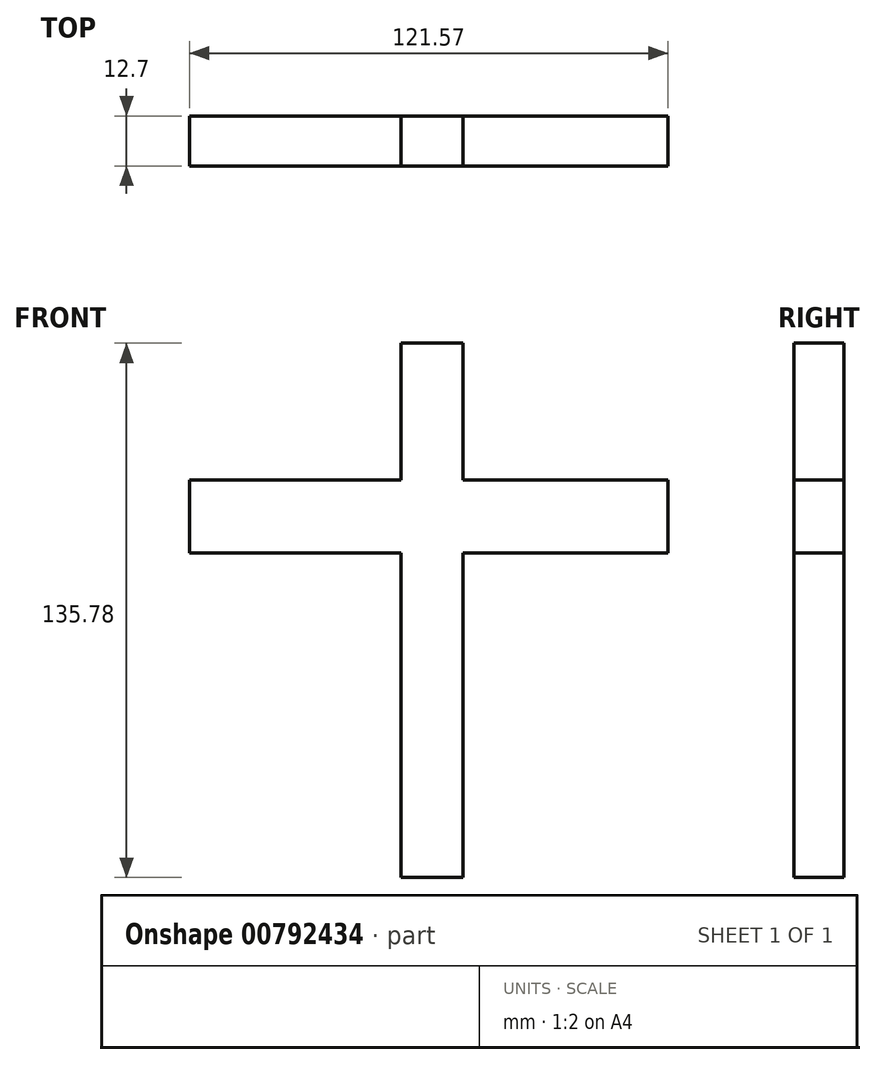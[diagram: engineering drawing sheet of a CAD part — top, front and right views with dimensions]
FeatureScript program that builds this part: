
annotation { "Feature Type Name" : "Feature", "Feature Type Description" : "" }
export const myFeature = defineFeature(function(context is Context, id is Id, definition is map)
    precondition{}
    {
        {
            var Q0;
            Q0=qCreatedBy(makeId("Front.planeOp"),FACE);
            var sketch = newSketch(context, id + "F0", { "sketchPlane" : qUnion([Q0])});
            skLineSegment(sketch, "E0.bottom", {"start": v(-7.7, 66.5) * mm, "end": v(8.1, 66.5) * mm});
            skLineSegment(sketch, "E0.top", {"start": v(-7.7, -69.27) * mm, "end": v(8.1, -69.27) * mm});
            skLineSegment(sketch, "E0.left", {"start": v(-7.7, 66.5) * mm, "end": v(-7.7, -69.27) * mm});
            skLineSegment(sketch, "E0.right", {"start": v(8.1, 66.5) * mm, "end": v(8.1, -69.27) * mm});
            skSolve(sketch);
        }
        {
            var Q0;
            Q0=qCreatedBy(makeId("Front.planeOp"),FACE);
            var sketch = newSketch(context, id + "F1", { "sketchPlane" : qUnion([Q0])});
            skLineSegment(sketch, "E1.bottom", {"start": v(-61.38, 31.77) * mm, "end": v(60.2, 31.77) * mm});
            skLineSegment(sketch, "E1.top", {"start": v(-61.38, 13.22) * mm, "end": v(60.2, 13.22) * mm});
            skLineSegment(sketch, "E1.left", {"start": v(-61.38, 31.77) * mm, "end": v(-61.38, 13.22) * mm});
            skLineSegment(sketch, "E1.right", {"start": v(60.2, 31.77) * mm, "end": v(60.2, 13.22) * mm});
            skSolve(sketch);
        }
        {
            var Q0;
            Q0=makeQuery(id+"F0.imprint","IMPRINT",FACE,{"disambiguationData":[TD([[makeQuery(id+"F0.imprint","IMPRINT",EDGE,{"derivedFrom":sQuery(id+"F0.wireOp",EDGE,"E0.bottom")}),-1.0]])]});
            extrude(context, id + "F2", {"entities" : qUnion([Q0]), "endBound" : BoundingType.SYMMETRIC, "depth" : 12.7 * mm, "offsetDistance" : 25.4 * mm});
        }
        {
            var Q0;
            Q0=makeQuery(id+"F1.imprint","IMPRINT",FACE,{"disambiguationData":[TD([[makeQuery(id+"F1.imprint","IMPRINT",EDGE,{"derivedFrom":sQuery(id+"F1.wireOp",EDGE,"E1.bottom")}),-1.0]])]});
            extrude(context, id + "F3", {"entities" : qUnion([Q0]), "operationType" : NewBodyOperationType.ADD, "endBound" : BoundingType.SYMMETRIC, "depth" : 12.7 * mm, "offsetDistance" : 25.4 * mm});
        }
    });
